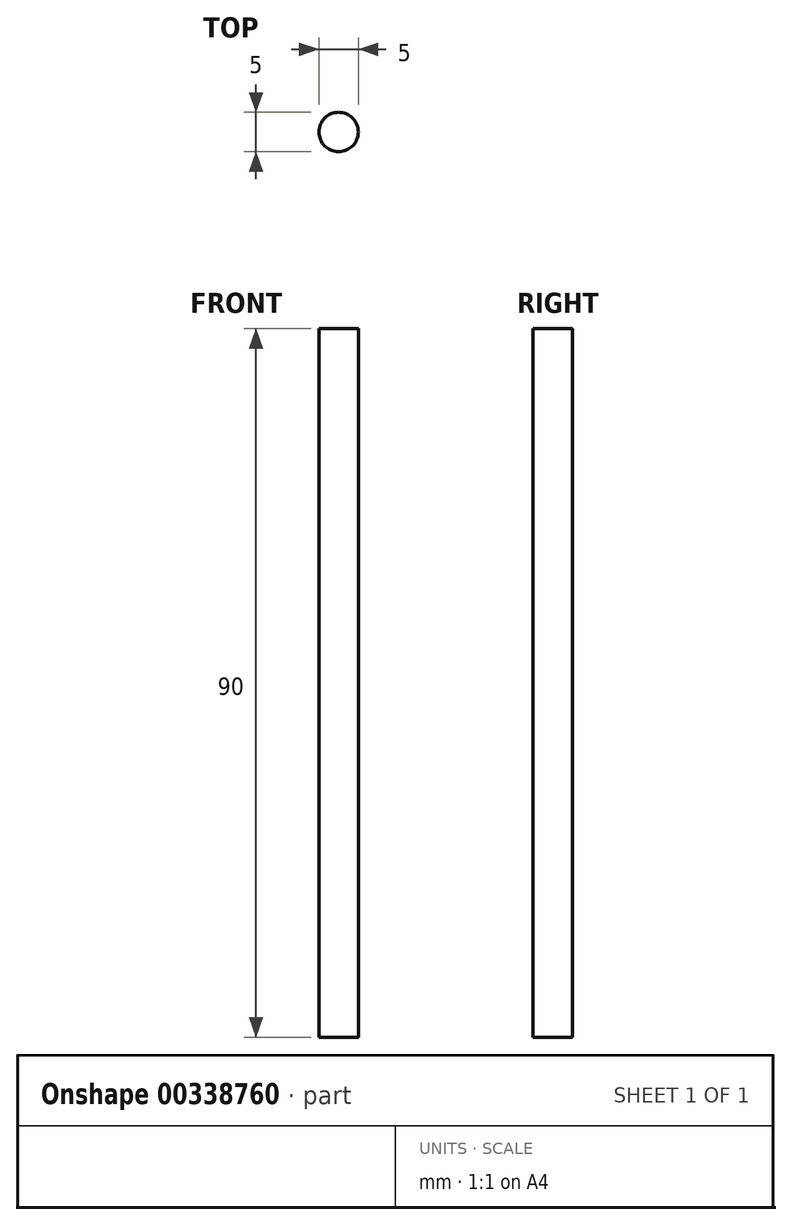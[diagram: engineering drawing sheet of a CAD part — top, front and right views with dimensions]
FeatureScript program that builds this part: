
annotation { "Feature Type Name" : "Feature", "Feature Type Description" : "" }
export const myFeature = defineFeature(function(context is Context, id is Id, definition is map)
    precondition{}
    {
        {
            var Q0;
            Q0=qCreatedBy(makeId("Top.planeOp"),FACE);
            var sketch = newSketch(context, id + "F0", { "sketchPlane" : qUnion([Q0])});
            skCircle(sketch, "E0", {"center": v(0, 0) * mm, "radius": 2.5 * mm});
            skSolve(sketch);
        }
        {
            var Q0;
            Q0=makeQuery(id+"F0.imprint","IMPRINT",FACE,{"disambiguationData":[TD([[makeQuery(id+"F0.imprint","IMPRINT",EDGE,{"derivedFrom":sQuery(id+"F0.wireOp",EDGE,"E0")}),1.0]])]});
            extrude(context, id + "F1", {"entities" : qUnion([Q0]), "depth" : 90 * mm});
        }
    });
